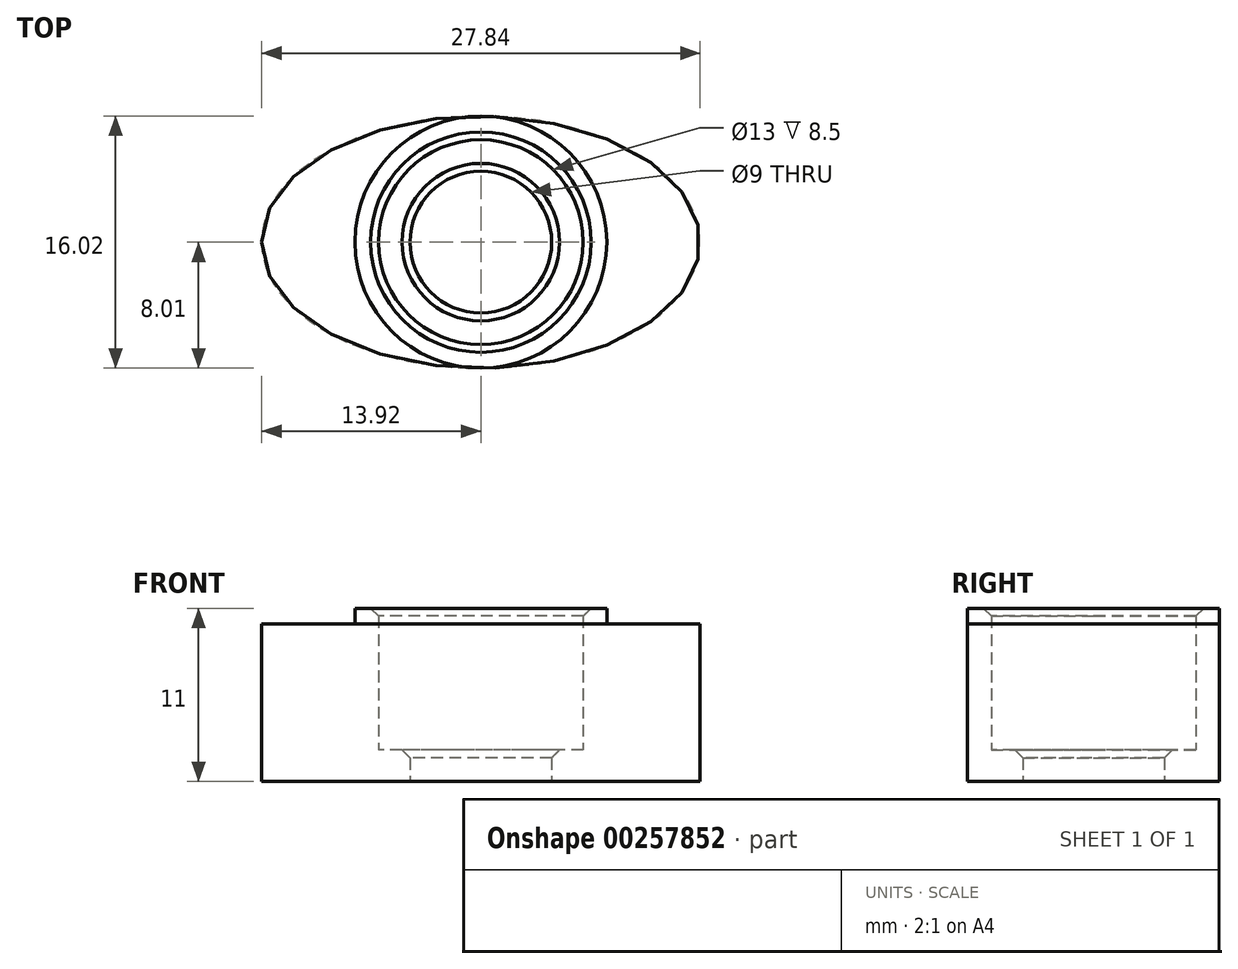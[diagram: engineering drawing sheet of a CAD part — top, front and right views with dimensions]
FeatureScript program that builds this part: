
annotation { "Feature Type Name" : "Feature", "Feature Type Description" : "" }
export const myFeature = defineFeature(function(context is Context, id is Id, definition is map)
    precondition{}
    {
        {
            var Q0;
            Q0=qCreatedBy(makeId("Top.planeOp"),FACE);
            var sketch = newSketch(context, id + "F0", { "sketchPlane" : qUnion([Q0])});
            skCircle(sketch, "E0", {"center": v(0, 0) * mm, "radius": 6.5 * mm});
            skCircle(sketch, "E1", {"center": v(0, 0) * mm, "radius": 4.5 * mm});
            skCircle(sketch, "E2", {"center": v(0, 0) * mm, "radius": 8 * mm});
            skEllipse(sketch, "E3", {"center": v(0, 0) * mm, "majorRadius": 8 * mm, "minorRadius": 13.92 * mm, "majorAxis": v(0, 1)});
            skSolve(sketch);
        }
        {
            var Q0;
            Q0=makeQuery(id+"F0.imprint","IMPRINT",FACE,{"disambiguationData":[TD([[makeQuery(id+"F0.imprint","IMPRINT",EDGE,{"derivedFrom":sQuery(id+"F0.wireOp",EDGE,"E0")}),-1.0]])]});
            extrude(context, id + "F1", {"entities" : qUnion([Q0]), "depth" : 11 * mm});
        }
        {
            var Q0;
            Q0=makeQuery(id+"F0.imprint","IMPRINT",FACE,{"disambiguationData":[TD([[makeQuery(id+"F0.imprint","IMPRINT",EDGE,{"derivedFrom":sQuery(id+"F0.wireOp",EDGE,"E0")}),1.0]])]});
            extrude(context, id + "F2", {"entities" : qUnion([Q0]), "operationType" : NewBodyOperationType.ADD, "depth" : 2 * mm});
        }
        {
            var Q0;
            Q0=makeQuery(id+"F0.imprint","IMPRINT",FACE,{"disambiguationData":[TD([[makeQuery(id+"F0.imprint","IMPRINT",EDGE,{"derivedFrom":sQuery(id+"F0.wireOp",EDGE,"E2")}),-1.0]])]});
            extrude(context, id + "F3", {"entities" : qUnion([Q0]), "operationType" : NewBodyOperationType.ADD, "depth" : 10 * mm});
        }
        {
            var Q0;
            Q0=makeQuery(id+"F1.opExtrude","CAP_EDGE",EDGE,{"disambiguationData":[OSD([sQuery(id+"F0.wireOp",EDGE,"E0")])],"isStart":false});
            var Q1;
            Q1=makeQuery(id+"F2.opExtrude","CAP_EDGE",EDGE,{"disambiguationData":[OSD([sQuery(id+"F0.wireOp",EDGE,"E1")])],"isStart":false});
            chamfer(context, id + "F4", {"entities" : qUnion([Q0, Q1]), "width" : 0.5 * mm, "tangentPropagation" : true});
        }
    });
